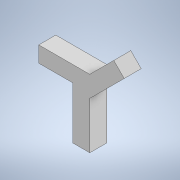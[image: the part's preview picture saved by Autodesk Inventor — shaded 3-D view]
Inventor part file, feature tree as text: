
AUTODESK INVENTOR PART (.ipt)
format: ipt  version: 2021.1 (Build 251245000, 245)  size: 113,152 bytes
history: native  units: in
note: dims shown in document units (in); Inventor stores cm internally (conversion verified against a paired STEP export)
features: extrude x3, sketch x3
ambient origin geometry x8: Origin, YZ Plane, XZ Plane, XY Plane, X Axis, Y Axis, Z Axis, Center Point
bodies: Solid1 (feature_tree)
feature tree (6):
  extrude  "Extrusion1"  Depth=4.0in TaperAngle=0.0deg
  extrude  "Extrusion3"  Depth=2.0in
  extrude  "Extrusion4"  Depth=1.0in TaperAngle=0.0deg
  sketch  "Sketch1"  dims[d0=1.0in d1=4.0in d2=0.0in]
  sketch  "Sketch3"  dims[d5=2.0in d6=0.0in d7=2.0in]
  sketch  "Sketch4"  dims[d8=45.0deg d9=1.0in d10=0.0in]
